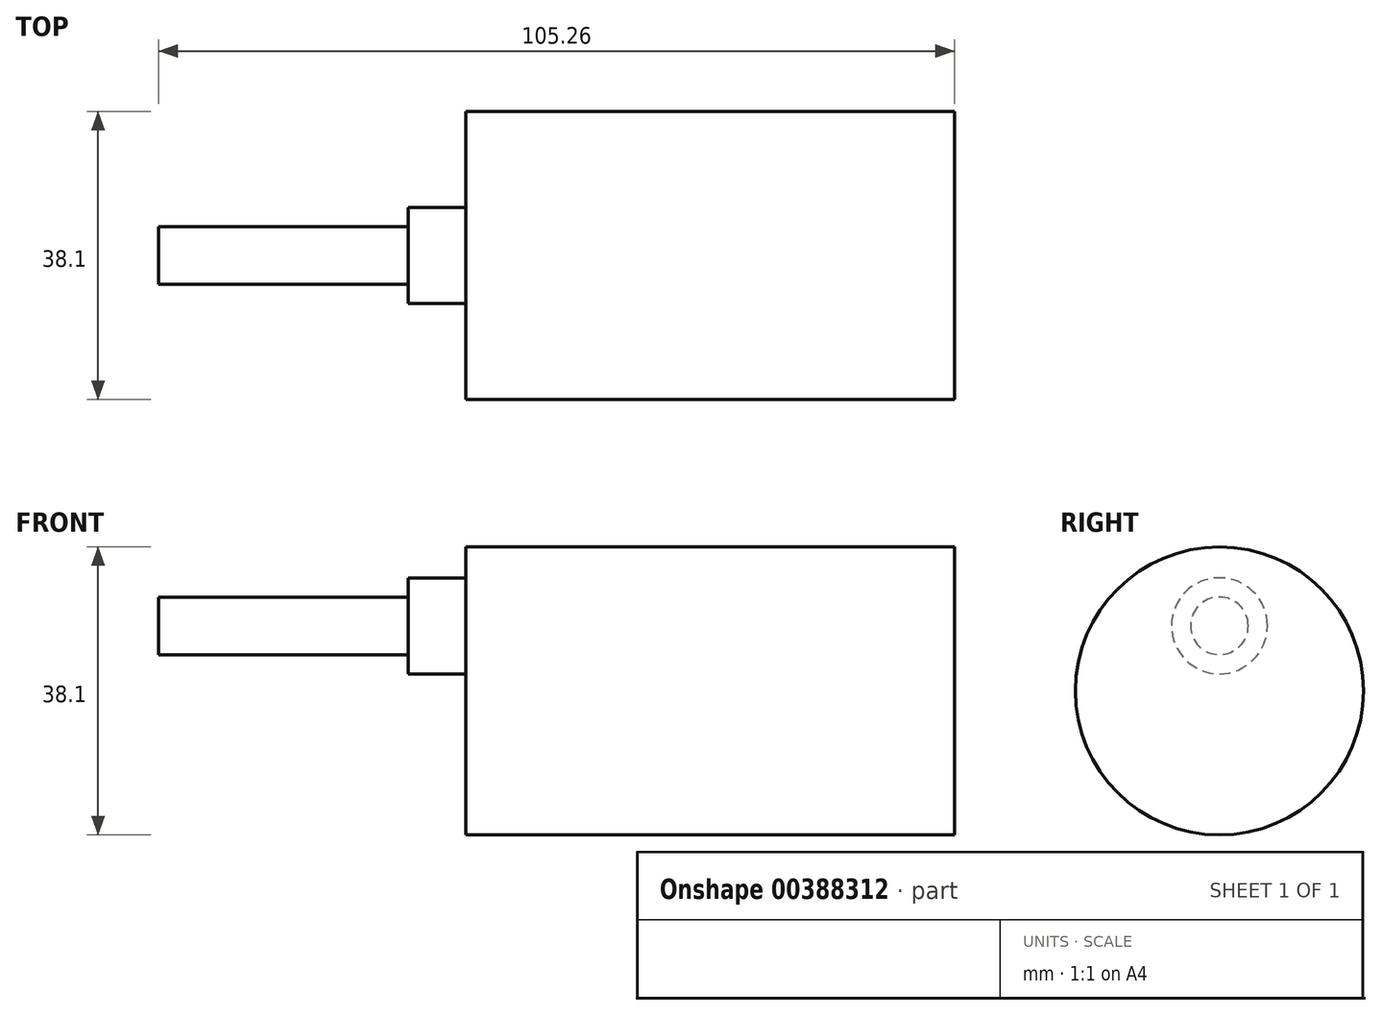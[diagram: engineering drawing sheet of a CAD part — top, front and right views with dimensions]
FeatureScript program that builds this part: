
annotation { "Feature Type Name" : "Feature", "Feature Type Description" : "" }
export const myFeature = defineFeature(function(context is Context, id is Id, definition is map)
    precondition{}
    {
        {
            var Q0;
            Q0=qCreatedBy(makeId("Front.planeOp"),FACE);
            var sketch = newSketch(context, id + "F0", { "sketchPlane" : qUnion([Q0])});
            skLineSegment(sketch, "E0", {"start": v(-26.21, 0) * mm, "end": v(38.4, 0) * mm});
            skLineSegment(sketch, "E1", {"start": v(38.4, 0) * mm, "end": v(38.4, 19.05) * mm});
            skLineSegment(sketch, "E2", {"start": v(38.4, 19.05) * mm, "end": v(-26.21, 19.05) * mm});
            skLineSegment(sketch, "E3", {"start": v(-26.21, 19.05) * mm, "end": v(-26.21, 0) * mm});
            skSolve(sketch);
        }
        {
            var Q0;
            Q0=makeQuery(id+"F0.imprint","IMPRINT",FACE,{"disambiguationData":[TD([[makeQuery(id+"F0.imprint","IMPRINT",EDGE,{"derivedFrom":sQuery(id+"F0.wireOp",EDGE,"E0")}),1.0]])]});
            var Q1;
            Q1=sQuery(id+"F0.wireOp",EDGE,"E0");
            revolve(context, id + "F1", {"entities" : qUnion([Q0]), "axis" : qUnion([Q1]), "revolveType" : RevolveType.FULL});
        }
        {
            var Q0;
            Q0=makeQuery(id+"F1.opRevolve","SWEPT_FACE",FACE,{"disambiguationData":[OSD([sQuery(id+"F0.wireOp",EDGE,"E3")])]});
            var sketch = newSketch(context, id + "F2", { "sketchPlane" : qUnion([Q0])});
            skCircle(sketch, "E4.0", {"center": v(0, 0) * mm, "radius": 19.05 * mm, "construction": true});
            skCircle(sketch, "E5", {"center": v(0, 8.6) * mm, "radius": 6.35 * mm});
            skSolve(sketch);
        }
        {
            var Q0;
            Q0=qSketchRegion(id+"F2",true);
            extrude(context, id + "F3", {"entities" : qUnion([Q0]), "operationType" : NewBodyOperationType.ADD, "depth" : 7.62 * mm});
        }
        {
            var Q0;
            Q0=makeQuery(id+"F3.opExtrude","CAP_FACE",FACE,{"disambiguationData":[OSD([sQuery(id+"F2.wireOp",EDGE,"E5")])],"isStart":false});
            var sketch = newSketch(context, id + "F4", { "sketchPlane" : qUnion([Q0])});
            skCircle(sketch, "E6", {"center": v(0, 8.6) * mm, "radius": 3.81 * mm});
            skSolve(sketch);
        }
        {
            var Q0;
            Q0=qSketchRegion(id+"F4",true);
            extrude(context, id + "F5", {"entities" : qUnion([Q0]), "operationType" : NewBodyOperationType.ADD, "depth" : 33.02 * mm});
        }
    });
